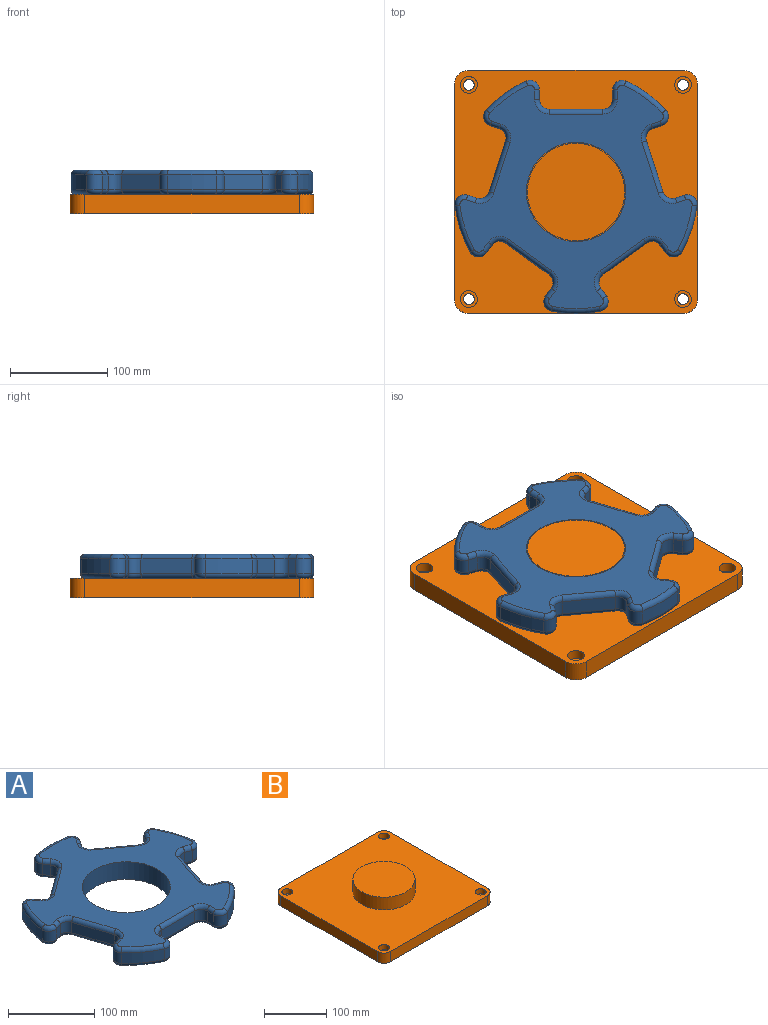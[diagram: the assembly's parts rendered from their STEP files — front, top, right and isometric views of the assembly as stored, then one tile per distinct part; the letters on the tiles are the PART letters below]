
ASSEMBLY  parts=2 mates=1
PART A: 123 faces, bbox 268.9x258.5x25 mm
  f0: plane 238.57x229.73mm, normal (0,0,1), area 21505.7mm2, adj f6,f43,f44,f45,f46,f47,f48,f49
  f1: plane 238.57x229.73mm, normal (0,0,-1), area 21505.7mm2, adj f6,f83,f84,f85,f86,f87,f88,f89
  f2: cylinder r=125mm len=40.68mm, axis (0,0,-1), area 759.5mm2, adj f13,f42,f51,f91
  f3: cylinder r=125mm len=47.82mm, axis (0,0,-1), area 759.5mm2, adj f35,f41,f67,f107
  f4: cylinder r=125mm len=50.29mm, axis (0,0,-1), area 759.5mm2, adj f28,f34,f82,f122
  f5: cylinder r=125mm len=47.82mm, axis (0,0,-1), area 759.5mm2, adj f21,f27,f66,f106
  f6: cylinder r=51mm len=102mm, axis (0,0,-1), area 8011.1mm2, adj f0,f1
  f7: cylinder r=125mm len=40.68mm, axis (0,0,-1), area 759.5mm2, adj f14,f20,f50,f90
  f8: plane 15x9.73mm, normal (-1,0,0), area 146mm2, adj f11,f14,f46,f86
  f9: plane 55x15mm, normal (0,-1,0), area 825mm2, adj f11,f12,f43,f83
  f10: plane 15x9.73mm, normal (1,0,0), area 146mm2, adj f12,f13,f47,f87
  f11: cylinder r=10mm len=15mm, axis (0,0,-1), area 235.6mm2, adj f8,f9,f44,f84
  f12: cylinder r=10mm len=15mm, axis (0,0,-1), area 235.6mm2, adj f9,f10,f45,f85
  f13: cylinder r=10mm len=15mm, axis (0,0,-1), area 299.5mm2, adj f2,f10,f49,f89
  f14: cylinder r=10mm len=15mm, axis (0,0,-1), area 299.5mm2, adj f7,f8,f48,f88
  f15: plane 15x9.26mm, normal (-0.31,-0.95,0), area 146mm2, adj f18,f21,f62,f102
  f16: plane 52.31x17mm, normal (0.95,-0.31,0), area 825mm2, adj f18,f19,f58,f98
  f17: plane 15x9.26mm, normal (0.31,0.95,0), area 146mm2, adj f19,f20,f54,f94
  f18: cylinder r=10mm len=15mm, axis (0,0,-1), area 235.6mm2, adj f15,f16,f60,f100
  f19: cylinder r=10mm len=15mm, axis (0,0,-1), area 235.6mm2, adj f16,f17,f56,f96
  f20: cylinder r=10mm len=16.25mm, axis (0,0,-1), area 299.5mm2, adj f7,f17,f52,f92
  f21: cylinder r=10mm len=15mm, axis (0,0,-1), area 299.5mm2, adj f5,f15,f64,f104
  f22: plane 15x7.87mm, normal (0.81,-0.59,0), area 146mm2, adj f25,f28,f78,f118
  f23: plane 44.5x32.33mm, normal (0.59,0.81,0), area 825mm2, adj f25,f26,f74,f114
  f24: plane 15x7.87mm, normal (-0.81,0.59,0), area 146mm2, adj f26,f27,f70,f110
  f25: cylinder r=10mm len=15mm, axis (0,0,-1), area 235.6mm2, adj f22,f23,f76,f116
  f26: cylinder r=10mm len=15mm, axis (0,0,-1), area 235.6mm2, adj f23,f24,f72,f112
  f27: cylinder r=10mm len=16.78mm, axis (0,0,-1), area 299.5mm2, adj f5,f24,f68,f108
  f28: cylinder r=10mm len=15.67mm, axis (0,0,-1), area 299.5mm2, adj f4,f22,f80,f120
  f29: plane 15x7.87mm, normal (0.81,0.59,0), area 146mm2, adj f32,f35,f71,f111
  f30: plane 44.5x32.33mm, normal (-0.59,0.81,0), area 825mm2, adj f32,f33,f75,f115
  f31: plane 15x7.87mm, normal (-0.81,-0.59,0), area 146mm2, adj f33,f34,f79,f119
  f32: cylinder r=10mm len=15mm, axis (0,0,-1), area 235.6mm2, adj f29,f30,f73,f113
  f33: cylinder r=10mm len=15mm, axis (0,0,-1), area 235.6mm2, adj f30,f31,f77,f117
  f34: cylinder r=10mm len=15.67mm, axis (0,0,-1), area 299.5mm2, adj f4,f31,f81,f121
  f35: cylinder r=10mm len=16.78mm, axis (0,0,-1), area 299.5mm2, adj f3,f29,f69,f109
  f36: plane 15x9.26mm, normal (-0.31,0.95,0), area 146mm2, adj f39,f42,f55,f95
  f37: plane 52.31x17mm, normal (-0.95,-0.31,0), area 825mm2, adj f39,f40,f59,f99
  f38: plane 15x9.26mm, normal (0.31,-0.95,0), area 146mm2, adj f40,f41,f63,f103
  f39: cylinder r=10mm len=15mm, axis (0,0,-1), area 235.6mm2, adj f36,f37,f57,f97
  f40: cylinder r=10mm len=15mm, axis (0,0,-1), area 235.6mm2, adj f37,f38,f61,f101
  f41: cylinder r=10mm len=15mm, axis (0,0,-1), area 299.5mm2, adj f3,f38,f65,f105
  f42: cylinder r=10mm len=16.25mm, axis (0,0,-1), area 299.5mm2, adj f2,f36,f53,f93
  f43: cylinder r=5mm len=55mm, axis (1,0,0), area 432mm2, adj f0,f9,f44,f45
  f44: torus R=15mm, axis (0,0,1), area 145.8mm2, adj f0,f11,f43,f46
  f45: torus R=15mm, axis (0,0,1), area 145.8mm2, adj f0,f12,f43,f47
  f46: cylinder r=5mm len=9.73mm, axis (0,-1,0), area 76.4mm2, adj f0,f8,f44,f48
  f47: cylinder r=5mm len=9.73mm, axis (0,1,0), area 76.4mm2, adj f0,f10,f45,f49
  f48: torus R=5mm, axis (0,0,1), area 128.3mm2, adj f0,f14,f46,f50
  f49: torus R=5mm, axis (0,0,1), area 128.3mm2, adj f0,f13,f47,f51
  f50: torus R=120mm, axis (0,0,1), area 391.9mm2, adj f0,f7,f48,f52
  f51: torus R=120mm, axis (0,0,1), area 391.9mm2, adj f0,f2,f49,f53
  f52: torus R=5mm, axis (0,0,1), area 128.3mm2, adj f0,f20,f50,f54
  f53: torus R=5mm, axis (0,0,1), area 128.3mm2, adj f0,f42,f51,f55
  f54: cylinder r=5mm len=10.8mm, axis (-0.95,0.31,0), area 76.4mm2, adj f0,f17,f52,f56
  f55: cylinder r=5mm len=10.8mm, axis (-0.95,-0.31,0), area 76.4mm2, adj f0,f36,f53,f57
  f56: torus R=15mm, axis (0,0,1), area 145.8mm2, adj f0,f19,f54,f58
  f57: torus R=15mm, axis (0,0,1), area 145.8mm2, adj f0,f39,f55,f59
  f58: cylinder r=5mm len=53.85mm, axis (0.31,0.95,0), area 432mm2, adj f0,f16,f56,f60
  f59: cylinder r=5mm len=53.85mm, axis (0.31,-0.95,0), area 432mm2, adj f0,f37,f57,f61
  f60: torus R=15mm, axis (0,0,1), area 145.8mm2, adj f0,f18,f58,f62
  f61: torus R=15mm, axis (0,0,1), area 145.8mm2, adj f0,f40,f59,f63
  f62: cylinder r=5mm len=10.8mm, axis (0.95,-0.31,0), area 76.4mm2, adj f0,f15,f60,f64
  f63: cylinder r=5mm len=10.8mm, axis (0.95,0.31,0), area 76.4mm2, adj f0,f38,f61,f65
  f64: torus R=5mm, axis (0,0,1), area 128.3mm2, adj f0,f21,f62,f66
  f65: torus R=5mm, axis (0,0,1), area 128.3mm2, adj f0,f41,f63,f67
  f66: torus R=120mm, axis (0,0,1), area 391.9mm2, adj f0,f5,f64,f68
  f67: torus R=120mm, axis (0,0,1), area 391.9mm2, adj f0,f3,f65,f69
  f68: torus R=5mm, axis (0,0,1), area 128.3mm2, adj f0,f27,f66,f70
  f69: torus R=5mm, axis (0,0,1), area 128.3mm2, adj f0,f35,f67,f71
  f70: cylinder r=5mm len=10.81mm, axis (-0.59,-0.81,0), area 76.4mm2, adj f0,f24,f68,f72
  f71: cylinder r=5mm len=10.81mm, axis (-0.59,0.81,0), area 76.4mm2, adj f0,f29,f69,f73
  f72: torus R=15mm, axis (0,0,1), area 145.8mm2, adj f0,f26,f70,f74
  f73: torus R=15mm, axis (0,0,1), area 145.8mm2, adj f0,f32,f71,f75
  f74: cylinder r=5mm len=47.44mm, axis (-0.81,0.59,0), area 432mm2, adj f0,f23,f72,f76
  f75: cylinder r=5mm len=47.44mm, axis (-0.81,-0.59,0), area 432mm2, adj f0,f30,f73,f77
  f76: torus R=15mm, axis (0,0,1), area 145.8mm2, adj f0,f25,f74,f78
  f77: torus R=15mm, axis (0,0,1), area 145.8mm2, adj f0,f33,f75,f79
  f78: cylinder r=5mm len=10.81mm, axis (0.59,0.81,0), area 76.4mm2, adj f0,f22,f76,f80
  f79: cylinder r=5mm len=10.81mm, axis (0.59,-0.81,0), area 76.4mm2, adj f0,f31,f77,f81
  f80: torus R=5mm, axis (0,0,1), area 128.3mm2, adj f0,f28,f78,f82
  f81: torus R=5mm, axis (0,0,1), area 128.3mm2, adj f0,f34,f79,f82
  f82: torus R=120mm, axis (0,0,1), area 391.9mm2, adj f0,f4,f80,f81
  f83: cylinder r=5mm len=55mm, axis (-1,0,0), area 432mm2, adj f1,f9,f84,f85
  f84: torus R=15mm, axis (0,0,1), area 145.8mm2, adj f1,f11,f83,f86
  f85: torus R=15mm, axis (0,0,1), area 145.8mm2, adj f1,f12,f83,f87
  f86: cylinder r=5mm len=9.73mm, axis (0,1,0), area 76.4mm2, adj f1,f8,f84,f88
  f87: cylinder r=5mm len=9.73mm, axis (0,-1,0), area 76.4mm2, adj f1,f10,f85,f89
  f88: torus R=5mm, axis (0,0,1), area 128.3mm2, adj f1,f14,f86,f90
  f89: torus R=5mm, axis (0,0,1), area 128.3mm2, adj f1,f13,f87,f91
  f90: torus R=120mm, axis (0,0,1), area 391.9mm2, adj f1,f7,f88,f92
  f91: torus R=120mm, axis (0,0,1), area 391.9mm2, adj f1,f2,f89,f93
  f92: torus R=5mm, axis (0,0,1), area 128.3mm2, adj f1,f20,f90,f94
  f93: torus R=5mm, axis (0,0,1), area 128.3mm2, adj f1,f42,f91,f95
  f94: cylinder r=5mm len=10.8mm, axis (0.95,-0.31,0), area 76.4mm2, adj f1,f17,f92,f96
  f95: cylinder r=5mm len=10.8mm, axis (0.95,0.31,0), area 76.4mm2, adj f1,f36,f93,f97
  f96: torus R=15mm, axis (0,0,1), area 145.8mm2, adj f1,f19,f94,f98
  f97: torus R=15mm, axis (0,0,1), area 145.8mm2, adj f1,f39,f95,f99
  f98: cylinder r=5mm len=53.85mm, axis (-0.31,-0.95,0), area 432mm2, adj f1,f16,f96,f100
  f99: cylinder r=5mm len=53.85mm, axis (-0.31,0.95,0), area 432mm2, adj f1,f37,f97,f101
  f100: torus R=15mm, axis (0,0,1), area 145.8mm2, adj f1,f18,f98,f102
  f101: torus R=15mm, axis (0,0,1), area 145.8mm2, adj f1,f40,f99,f103
  f102: cylinder r=5mm len=10.8mm, axis (-0.95,0.31,0), area 76.4mm2, adj f1,f15,f100,f104
  f103: cylinder r=5mm len=10.8mm, axis (-0.95,-0.31,0), area 76.4mm2, adj f1,f38,f101,f105
  f104: torus R=5mm, axis (0,0,1), area 128.3mm2, adj f1,f21,f102,f106
  f105: torus R=5mm, axis (0,0,1), area 128.3mm2, adj f1,f41,f103,f107
  f106: torus R=120mm, axis (0,0,1), area 391.9mm2, adj f1,f5,f104,f108
  f107: torus R=120mm, axis (0,0,1), area 391.9mm2, adj f1,f3,f105,f109
  f108: torus R=5mm, axis (0,0,1), area 128.3mm2, adj f1,f27,f106,f110
  f109: torus R=5mm, axis (0,0,1), area 128.3mm2, adj f1,f35,f107,f111
  f110: cylinder r=5mm len=10.81mm, axis (0.59,0.81,0), area 76.4mm2, adj f1,f24,f108,f112
  f111: cylinder r=5mm len=10.81mm, axis (0.59,-0.81,0), area 76.4mm2, adj f1,f29,f109,f113
  f112: torus R=15mm, axis (0,0,1), area 145.8mm2, adj f1,f26,f110,f114
  f113: torus R=15mm, axis (0,0,1), area 145.8mm2, adj f1,f32,f111,f115
  f114: cylinder r=5mm len=47.44mm, axis (0.81,-0.59,0), area 432mm2, adj f1,f23,f112,f116
  f115: cylinder r=5mm len=47.44mm, axis (0.81,0.59,0), area 432mm2, adj f1,f30,f113,f117
  f116: torus R=15mm, axis (0,0,1), area 145.8mm2, adj f1,f25,f114,f118
  f117: torus R=15mm, axis (0,0,1), area 145.8mm2, adj f1,f33,f115,f119
  f118: cylinder r=5mm len=10.81mm, axis (-0.59,-0.81,0), area 76.4mm2, adj f1,f22,f116,f120
  f119: cylinder r=5mm len=10.81mm, axis (-0.59,0.81,0), area 76.4mm2, adj f1,f31,f117,f121
  f120: torus R=5mm, axis (0,0,1), area 128.3mm2, adj f1,f28,f118,f122
  f121: torus R=5mm, axis (0,0,1), area 128.3mm2, adj f1,f34,f119,f122
  f122: torus R=120mm, axis (0,0,1), area 391.9mm2, adj f1,f4,f120,f121
PART B: 24 faces, bbox 250x250x45 mm
  f0: plane 220x20mm, normal (1,0,0), area 4400mm2, adj f4,f5,f8,f11
  f1: plane 220x20mm, normal (0,1,0), area 4400mm2, adj f4,f5,f8,f9
  f2: plane 220x20mm, normal (-1,0,0), area 4400mm2, adj f4,f5,f9,f10
  f3: plane 220x20mm, normal (0,-1,0), area 4400mm2, adj f4,f5,f10,f11
  f4: plane 250x250mm, normal (0,0,1), area 53518.1mm2, adj f0,f1,f2,f3,f6,f8,f9,f10
  f5: plane 250x250mm, normal (0,0,-1), area 61926.7mm2, adj f0,f1,f2,f3,f8,f9,f10,f11
  f6: cylinder r=50mm len=100mm, axis (0,0,-1), area 7854mm2, adj f4,f7
  f7: plane 100x100mm, normal (0,0,1), area 7854mm2, adj f6
  f8: cylinder r=15mm len=20mm, axis (0,0,-1), area 471.2mm2, adj f0,f1,f4,f5
  f9: cylinder r=15mm len=20mm, axis (0,0,1), area 471.2mm2, adj f1,f2,f4,f5
  f10: cylinder r=15mm len=20mm, axis (0,0,-1), area 471.2mm2, adj f2,f3,f4,f5
  f11: cylinder r=15mm len=20mm, axis (0,0,1), area 471.2mm2, adj f0,f3,f4,f5
  f12: cylinder r=5.5mm len=11mm, axis (0,0,1), area 345.6mm2, adj f5,f13
  f13: plane 17.25x17.25mm, normal (0,0,1), area 138.7mm2, adj f12,f14
  f14: cylinder r=8.62mm len=17.25mm, axis (0,0,1), area 541.9mm2, adj f4,f13
  f15: cylinder r=5.5mm len=11mm, axis (0,0,1), area 345.6mm2, adj f5,f16
  f16: plane 17.25x17.25mm, normal (0,0,1), area 138.7mm2, adj f15,f17
  f17: cylinder r=8.62mm len=17.25mm, axis (0,0,1), area 541.9mm2, adj f4,f16
  f18: cylinder r=5.5mm len=11mm, axis (0,0,1), area 345.6mm2, adj f5,f19
  f19: plane 17.25x17.25mm, normal (0,0,1), area 138.7mm2, adj f18,f20
  f20: cylinder r=8.62mm len=17.25mm, axis (0,0,1), area 541.9mm2, adj f4,f19
  f21: cylinder r=5.5mm len=11mm, axis (0,0,1), area 345.6mm2, adj f5,f22
  f22: plane 17.25x17.25mm, normal (0,0,1), area 138.7mm2, adj f21,f23
  f23: cylinder r=8.62mm len=17.25mm, axis (0,0,1), area 541.9mm2, adj f4,f22
PLACE A rot(axis=(1,0,0),180deg) t=(-16.03,-23.17,21.62)mm
PLACE B t=(-16.03,-23.17,-43.38)mm
MATE revolute A.f2 <-> B.f6  axis (0,0,1) through (-16.03,-23.17,-23.38)mm
